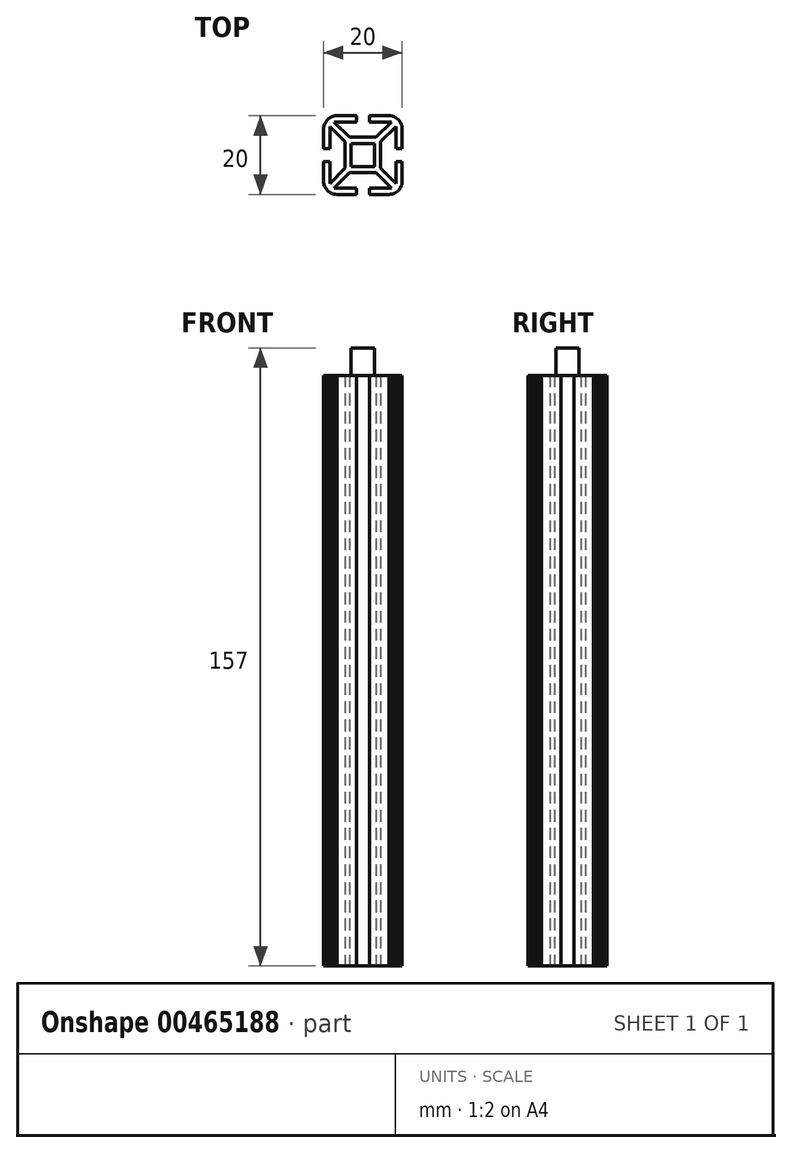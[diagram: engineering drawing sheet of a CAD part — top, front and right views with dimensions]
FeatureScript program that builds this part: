
annotation { "Feature Type Name" : "Feature", "Feature Type Description" : "" }
export const myFeature = defineFeature(function(context is Context, id is Id, definition is map)
    precondition{}
    {
        {
            var Q0;
            Q0=qCreatedBy(makeId("Top.planeOp"),FACE);
            var sketch = newSketch(context, id + "F0", { "sketchPlane" : qUnion([Q0])});
            skLineSegment(sketch, "E0", {"start": v(-9, 9) * mm, "end": v(-9.3, 8.66) * mm});
            skLineSegment(sketch, "E1", {"start": v(-9.54, 8.3) * mm, "end": v(-9.74, 7.9) * mm});
            skLineSegment(sketch, "E2", {"start": v(8.3, -9.54) * mm, "end": v(8.66, -9.3) * mm});
            skLineSegment(sketch, "E3", {"start": v(9.88, -7.47) * mm, "end": v(9.97, -7.03) * mm});
            skLineSegment(sketch, "E4", {"start": v(8.66, 9.3) * mm, "end": v(8.3, 9.54) * mm});
            skLineSegment(sketch, "E5", {"start": v(9.3, -8.66) * mm, "end": v(9.54, -8.3) * mm});
            skLineSegment(sketch, "E6", {"start": v(-8.3, 9.54) * mm, "end": v(-8.66, 9.3) * mm});
            skLineSegment(sketch, "E7", {"start": v(9.54, 8.3) * mm, "end": v(9.3, 8.66) * mm});
            skLineSegment(sketch, "E8", {"start": v(-4.5, 3.37) * mm, "end": v(-4.5, -3.37) * mm});
            skLineSegment(sketch, "E9", {"start": v(-10, -6.59) * mm, "end": v(-9.97, -7.03) * mm});
            skLineSegment(sketch, "E10", {"start": v(-10, 1.65) * mm, "end": v(-10, 6.59) * mm});
            skLineSegment(sketch, "E11", {"start": v(-10, -6.59) * mm, "end": v(-10, -1.65) * mm});
            skLineSegment(sketch, "E12", {"start": v(-9.97, -7.03) * mm, "end": v(-9.88, -7.47) * mm});
            skLineSegment(sketch, "E13", {"start": v(-9.88, -7.47) * mm, "end": v(-9.74, -7.9) * mm});
            skLineSegment(sketch, "E14", {"start": v(-9.74, -7.9) * mm, "end": v(-9.54, -8.3) * mm});
            skLineSegment(sketch, "E15", {"start": v(-9.54, -8.3) * mm, "end": v(-9.3, -8.66) * mm});
            skLineSegment(sketch, "E16", {"start": v(-9.3, -8.66) * mm, "end": v(-9, -9) * mm});
            skLineSegment(sketch, "E17", {"start": v(-9, -9) * mm, "end": v(-8.66, -9.3) * mm});
            skLineSegment(sketch, "E18", {"start": v(-8.66, -9.3) * mm, "end": v(-8.3, -9.54) * mm});
            skLineSegment(sketch, "E19", {"start": v(-8.3, -9.54) * mm, "end": v(-7.9, -9.74) * mm});
            skLineSegment(sketch, "E20", {"start": v(-7.9, -9.74) * mm, "end": v(-7.47, -9.88) * mm});
            skLineSegment(sketch, "E21", {"start": v(-7.47, -9.88) * mm, "end": v(-7.03, -9.97) * mm});
            skLineSegment(sketch, "E22", {"start": v(-7.03, -9.97) * mm, "end": v(-6.59, -10) * mm});
            skLineSegment(sketch, "E23", {"start": v(-1.65, -10) * mm, "end": v(-6.59, -10) * mm});
            skLineSegment(sketch, "E24", {"start": v(-3.37, -4.5) * mm, "end": v(3.37, -4.5) * mm});
            skLineSegment(sketch, "E25", {"start": v(6.59, -10) * mm, "end": v(1.65, -10) * mm});
            skLineSegment(sketch, "E26", {"start": v(6.59, -10) * mm, "end": v(7.03, -9.97) * mm});
            skLineSegment(sketch, "E27", {"start": v(7.03, -9.97) * mm, "end": v(7.47, -9.88) * mm});
            skLineSegment(sketch, "E28", {"start": v(7.47, -9.88) * mm, "end": v(7.9, -9.74) * mm});
            skLineSegment(sketch, "E29", {"start": v(7.9, -9.74) * mm, "end": v(8.3, -9.54) * mm});
            skLineSegment(sketch, "E30", {"start": v(8.66, -9.3) * mm, "end": v(9, -9) * mm});
            skLineSegment(sketch, "E31", {"start": v(9, -9) * mm, "end": v(9.3, -8.66) * mm});
            skLineSegment(sketch, "E32", {"start": v(9.54, -8.3) * mm, "end": v(9.74, -7.9) * mm});
            skLineSegment(sketch, "E33", {"start": v(9.74, -7.9) * mm, "end": v(9.88, -7.47) * mm});
            skLineSegment(sketch, "E34", {"start": v(9.97, -7.03) * mm, "end": v(10, -6.59) * mm});
            skLineSegment(sketch, "E35", {"start": v(10, -1.65) * mm, "end": v(10, -6.59) * mm});
            skLineSegment(sketch, "E36", {"start": v(4.5, -3.37) * mm, "end": v(4.5, 3.37) * mm});
            skLineSegment(sketch, "E37", {"start": v(10, 6.59) * mm, "end": v(10, 1.65) * mm});
            skLineSegment(sketch, "E38", {"start": v(10, 6.59) * mm, "end": v(9.97, 7.03) * mm});
            skLineSegment(sketch, "E39", {"start": v(9.97, 7.03) * mm, "end": v(9.88, 7.47) * mm});
            skLineSegment(sketch, "E40", {"start": v(9.88, 7.47) * mm, "end": v(9.74, 7.9) * mm});
            skLineSegment(sketch, "E41", {"start": v(9.74, 7.9) * mm, "end": v(9.54, 8.3) * mm});
            skLineSegment(sketch, "E42", {"start": v(9.3, 8.66) * mm, "end": v(9, 9) * mm});
            skLineSegment(sketch, "E43", {"start": v(9, 9) * mm, "end": v(8.66, 9.3) * mm});
            skLineSegment(sketch, "E44", {"start": v(8.3, 9.54) * mm, "end": v(7.9, 9.74) * mm});
            skLineSegment(sketch, "E45", {"start": v(7.9, 9.74) * mm, "end": v(7.47, 9.88) * mm});
            skLineSegment(sketch, "E46", {"start": v(7.47, 9.88) * mm, "end": v(7.03, 9.97) * mm});
            skLineSegment(sketch, "E47", {"start": v(7.03, 9.97) * mm, "end": v(6.59, 10) * mm});
            skLineSegment(sketch, "E48", {"start": v(1.65, 10) * mm, "end": v(6.59, 10) * mm});
            skLineSegment(sketch, "E49", {"start": v(3.37, 4.5) * mm, "end": v(-3.37, 4.5) * mm});
            skLineSegment(sketch, "E50", {"start": v(-6.59, 10) * mm, "end": v(-7.03, 9.97) * mm});
            skLineSegment(sketch, "E51", {"start": v(-7.03, 9.97) * mm, "end": v(-7.47, 9.88) * mm});
            skLineSegment(sketch, "E52", {"start": v(-7.47, 9.88) * mm, "end": v(-7.9, 9.74) * mm});
            skLineSegment(sketch, "E53", {"start": v(-7.9, 9.74) * mm, "end": v(-8.3, 9.54) * mm});
            skLineSegment(sketch, "E54", {"start": v(-8.66, 9.3) * mm, "end": v(-9, 9) * mm});
            skLineSegment(sketch, "E55", {"start": v(-9.3, 8.66) * mm, "end": v(-9.54, 8.3) * mm});
            skLineSegment(sketch, "E56", {"start": v(-9.74, 7.9) * mm, "end": v(-9.88, 7.47) * mm});
            skLineSegment(sketch, "E57", {"start": v(-9.88, 7.47) * mm, "end": v(-9.97, 7.03) * mm});
            skLineSegment(sketch, "E58", {"start": v(-9.97, 7.03) * mm, "end": v(-10, 6.59) * mm});
            skLineSegment(sketch, "E59", {"start": v(-4.5, -3.37) * mm, "end": v(-8.4, -7.27) * mm});
            skLineSegment(sketch, "E60", {"start": v(-8.4, -1.65) * mm, "end": v(-10, -1.65) * mm});
            skLineSegment(sketch, "E61", {"start": v(-8.4, -7.27) * mm, "end": v(-8.4, -1.65) * mm});
            skLineSegment(sketch, "E62", {"start": v(-3.37, -4.5) * mm, "end": v(-7.27, -8.4) * mm});
            skLineSegment(sketch, "E63", {"start": v(-1.65, -8.4) * mm, "end": v(-1.65, -10) * mm});
            skLineSegment(sketch, "E64", {"start": v(-7.27, -8.4) * mm, "end": v(-1.65, -8.4) * mm});
            skLineSegment(sketch, "E65", {"start": v(-4.5, 3.37) * mm, "end": v(-8.4, 7.27) * mm});
            skLineSegment(sketch, "E66", {"start": v(-8.4, 1.65) * mm, "end": v(-10, 1.65) * mm});
            skLineSegment(sketch, "E67", {"start": v(-8.4, 7.27) * mm, "end": v(-8.4, 1.65) * mm});
            skLineSegment(sketch, "E68", {"start": v(-3.37, 4.5) * mm, "end": v(-7.27, 8.4) * mm});
            skLineSegment(sketch, "E69", {"start": v(-1.65, 8.4) * mm, "end": v(-1.65, 10) * mm});
            skLineSegment(sketch, "E70", {"start": v(-7.27, 8.4) * mm, "end": v(-1.65, 8.4) * mm});
            skLineSegment(sketch, "E71", {"start": v(3.37, 4.5) * mm, "end": v(7.27, 8.4) * mm});
            skLineSegment(sketch, "E72", {"start": v(1.65, 8.4) * mm, "end": v(1.65, 10) * mm});
            skLineSegment(sketch, "E73", {"start": v(7.27, 8.4) * mm, "end": v(1.65, 8.4) * mm});
            skLineSegment(sketch, "E74", {"start": v(4.5, 3.37) * mm, "end": v(8.4, 7.27) * mm});
            skLineSegment(sketch, "E75", {"start": v(8.4, 1.65) * mm, "end": v(10, 1.65) * mm});
            skLineSegment(sketch, "E76", {"start": v(8.4, 7.27) * mm, "end": v(8.4, 1.65) * mm});
            skLineSegment(sketch, "E77", {"start": v(4.5, -3.37) * mm, "end": v(8.4, -7.27) * mm});
            skLineSegment(sketch, "E78", {"start": v(8.4, -1.65) * mm, "end": v(10, -1.65) * mm});
            skLineSegment(sketch, "E79", {"start": v(8.4, -7.27) * mm, "end": v(8.4, -1.65) * mm});
            skLineSegment(sketch, "E80", {"start": v(3.37, -4.5) * mm, "end": v(7.27, -8.4) * mm});
            skLineSegment(sketch, "E81", {"start": v(1.65, -8.4) * mm, "end": v(1.65, -10) * mm});
            skLineSegment(sketch, "E82", {"start": v(7.27, -8.4) * mm, "end": v(1.65, -8.4) * mm});
            skLineSegment(sketch, "E83", {"start": v(-1.65, 10) * mm, "end": v(-6.59, 10) * mm});
            skSolve(sketch);
        }
        {
            var Q0;
            Q0 = qSketchRegion(id + "F0", true);
            extrude(context, id + "F1", {"entities" : qUnion([Q0]), "depth" : 150 * mm});
        }
        {
            var Q0;
            Q0=qCreatedBy(makeId("Top.planeOp"),FACE);
            var sketch = newSketch(context, id + "F2", { "sketchPlane" : qUnion([Q0])});
            skLineSegment(sketch, "E84.bottom", {"start": v(2.95, 2.95) * mm, "end": v(-2.95, 2.95) * mm});
            skLineSegment(sketch, "E84.top", {"start": v(2.95, -2.95) * mm, "end": v(-2.95, -2.95) * mm});
            skLineSegment(sketch, "E84.left", {"start": v(2.95, 2.95) * mm, "end": v(2.95, -2.95) * mm});
            skLineSegment(sketch, "E84.right", {"start": v(-2.95, 2.95) * mm, "end": v(-2.95, -2.95) * mm});
            skPoint(sketch, "E84.middle", {"position": v(0, 0) * mm});
            skSolve(sketch);
        }
        {
            var Q0;
            Q0 = qSketchRegion(id + "F2", true);
            extrude(context, id + "F3", {"entities" : qUnion([Q0]), "operationType" : NewBodyOperationType.ADD, "depth" : 157 * mm, "hasSecondDirection" : true, "secondDirectionOppositeDirection" : false, "secondDirectionDepth" : 150 * mm});
        }
    });
